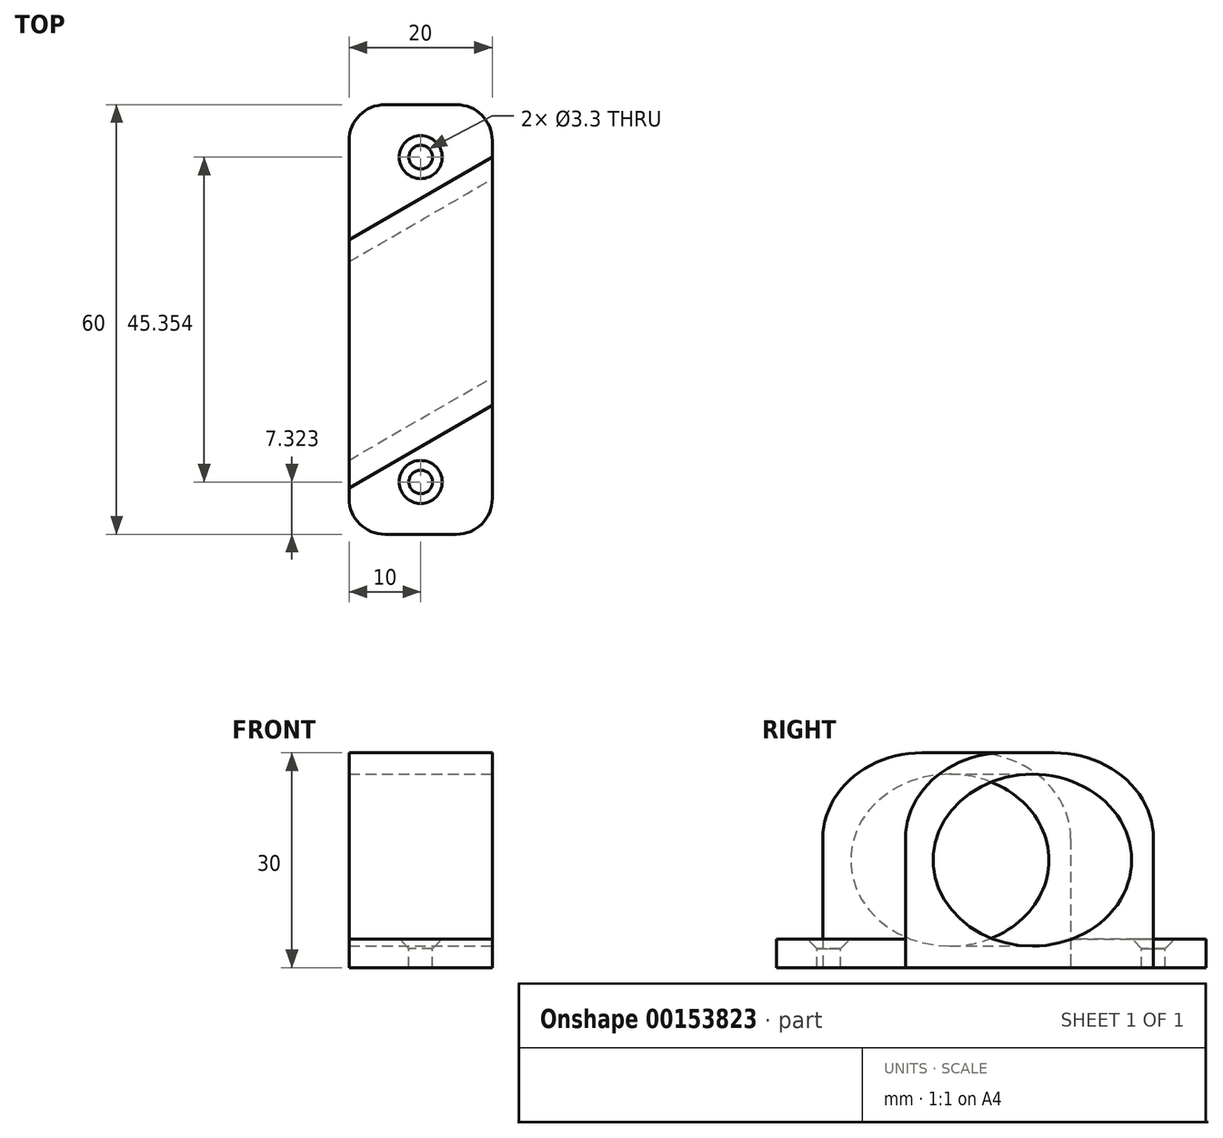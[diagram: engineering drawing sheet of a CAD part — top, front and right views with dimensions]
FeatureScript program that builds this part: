
annotation { "Feature Type Name" : "Feature", "Feature Type Description" : "" }
export const myFeature = defineFeature(function(context is Context, id is Id, definition is map)
    precondition{}
    {
        {
            var Q0;
            Q0=qCreatedBy(makeId("Top.planeOp"),FACE);
            var sketch = newSketch(context, id + "F0", { "sketchPlane" : qUnion([Q0])});
            skLineSegment(sketch, "E0.bottom", {"start": v(-10, 30) * mm, "end": v(10, 30) * mm});
            skLineSegment(sketch, "E0.top", {"start": v(-10, -30) * mm, "end": v(10, -30) * mm});
            skLineSegment(sketch, "E0.left", {"start": v(-10, 30) * mm, "end": v(-10, -30) * mm});
            skLineSegment(sketch, "E0.right", {"start": v(10, 30) * mm, "end": v(10, -30) * mm});
            skPoint(sketch, "E0.middle", {"position": v(0, 0) * mm});
            skLineSegment(sketch, "E1", {"start": v(-10, 11.13) * mm, "end": v(10, 22.68) * mm});
            skLineSegment(sketch, "E2", {"start": v(10, -11.96) * mm, "end": v(-10, -23.51) * mm});
            skPoint(sketch, "E3.orphan", {"position": v(-29.28, 0) * mm});
            skPoint(sketch, "E4.orphan", {"position": v(-29.28, -34.64) * mm});
            skSolve(sketch);
        }
        {
            var Q0;
            {var subQ0=sQuery(id+"F0.wireOp",EDGE,"E0.bottom");Q0=makeQuery(id+"F0.imprint","IMPRINT",FACE,{"disambiguationData":[TD([[makeQuery(id+"F0.imprint","IMPRINT",EDGE,{"derivedFrom":subQ0}),-1.0]])]});}
            var Q1;
            {var subQ0=sQuery(id+"F0.wireOp",EDGE,"E0.top");Q1=makeQuery(id+"F0.imprint","IMPRINT",FACE,{"disambiguationData":[TD([[makeQuery(id+"F0.imprint","IMPRINT",EDGE,{"derivedFrom":subQ0}),1.0]])]});}
            extrude(context, id + "F1", {"entities" : qUnion([Q0, Q1]), "depth" : 4 * mm});
        }
        {
            var Q0;
            {var subQ0=sQuery(id+"F0.wireOp",EDGE,"E1");Q0=makeQuery(id+"F0.imprint","IMPRINT",FACE,{"disambiguationData":[TD([[makeQuery(id+"F0.imprint","IMPRINT",EDGE,{"derivedFrom":subQ0}),-1.0]])]});}
            extrude(context, id + "F2", {"entities" : qUnion([Q0]), "depth" : 30 * mm});
        }
        {
            var Q0;
            Q0=makeQuery(id+"F2.opExtrude","SWEPT_FACE",FACE,{"disambiguationData":[OSD([sQuery(id+"F0.wireOp",EDGE,"E1")])]});
            var sketch = newSketch(context, id + "F3", { "sketchPlane" : qUnion([Q0])});
            skLineSegment(sketch, "E5.bottom", {"start": v(-20, 15.59) * mm, "end": v(-1.97, 15.59) * mm});
            skLineSegment(sketch, "E5.top", {"start": v(-20, 27.37) * mm, "end": v(-1.97, 27.37) * mm});
            skLineSegment(sketch, "E5.left", {"start": v(-20, 15.59) * mm, "end": v(-20, 27.37) * mm});
            skLineSegment(sketch, "E5.right", {"start": v(-1.97, 15.59) * mm, "end": v(-1.97, 27.37) * mm});
            skPoint(sketch, "E5.middle", {"position": v(-10.98, 21.48) * mm});
            skSolve(sketch);
        }
        {
            var Q0;
            Q0=makeQuery(id+"F3.imprint","IMPRINT",FACE,{"disambiguationData":[TD([[makeQuery(id+"F3.imprint","IMPRINT",EDGE,{"derivedFrom":sQuery(id+"F3.wireOp",EDGE,"E5.bottom")}),1.0]])]});
            extrude(context, id + "F4", {"entities" : qUnion([Q0]), "operationType" : NewBodyOperationType.ADD, "depth" : 25 * mm});
        }
        {
            var Q0;
            Q0=makeQuery(id+"F4.opExtrude","SWEPT_FACE",FACE,{"disambiguationData":[OSD([sQuery(id+"F3.wireOp",EDGE,"E5.left")])]});
            cPlane(context, id + "F5", {"entities" : qUnion([Q0]), "cplaneType" : CPlaneType.OFFSET, "offset" : 0 * mm, "width" : 150 * mm, "height" : 150 * mm});
        }
        {
            var Q0;
            Q0=qCreatedBy(id+"F5.planeOp",FACE);
            var sketch = newSketch(context, id + "F6", { "sketchPlane" : qUnion([Q0])});
            skLineSegment(sketch, "E6", {"start": v(0, 0) * mm, "end": v(0, 30) * mm, "construction": true});
            skLineSegment(sketch, "E7.0", {"start": v(14.64, 30) * mm, "end": v(-15.36, 30) * mm});
            skPoint(sketch, "E8", {"position": v(0, 15) * mm});
            skCircle(sketch, "E9", {"center": v(0, 15) * mm, "radius": 12 * mm});
            skSolve(sketch);
        }
        {
            var Q0;
            Q0=qSketchRegion(id+"F6",true);
            extrude(context, id + "F7", {"entities" : qUnion([Q0]), "operationType" : NewBodyOperationType.REMOVE, "oppositeDirection" : true, "depth" : 67.5 * mm, "hasSecondDirection" : true, "secondDirectionOppositeDirection" : false, "secondDirectionDepth" : 25 * mm});
        }
        {
            var Q0;
            Q0=makeQuery(id+"F4.opExtrude","SWEPT_FACE",FACE,{"disambiguationData":[OSD([sQuery(id+"F3.wireOp",EDGE,"E5.left")])]});
            extrude(context, id + "F8", {"entities" : qUnion([Q0]), "operationType" : NewBodyOperationType.REMOVE, "oppositeDirection" : true, "depth" : 25 * mm});
        }
        {
            var Q0;
            Q0=makeQuery(id+"F1.opExtrude","CAP_FACE",FACE,{"disambiguationData":[OSD([sQuery(id+"F0.wireOp",EDGE,"E0.bottom"),sQuery(id+"F0.wireOp",EDGE,"E0.left"),sQuery(id+"F0.wireOp",EDGE,"E0.right"),sQuery(id+"F0.wireOp",EDGE,"E1")])],"isStart":false});
            var sketch = newSketch(context, id + "F9", { "sketchPlane" : qUnion([Q0])});
            skLineSegment(sketch, "E10", {"start": v(10, 22.68) * mm, "end": v(-10, 22.68) * mm, "construction": true});
            skPoint(sketch, "E11", {"position": v(0, 22.68) * mm});
            skPoint(sketch, "E12.MirrorP", {"position": v(0, -22.68) * mm});
            skSolve(sketch);
        }
        {
            var Q0;
            Q0=sQuery(id+"F9.wireOp",VERTEX,"E11");
            var Q1;
            Q1=sQuery(id+"F9.wireOp",VERTEX,"E12.MirrorP");
            var Q2;
            Q2=makeQuery(id+"F1.opExtrude","SWEPT_BODY",BODY,{"disambiguationData":[OSD([sQuery(id+"F0.wireOp",EDGE,"E0.bottom"),sQuery(id+"F0.wireOp",EDGE,"E0.left"),sQuery(id+"F0.wireOp",EDGE,"E0.right"),sQuery(id+"F0.wireOp",EDGE,"E1")])]});
            var Q3;
            Q3=makeQuery(id+"F1.opExtrude","SWEPT_BODY",BODY,{"disambiguationData":[OSD([sQuery(id+"F0.wireOp",EDGE,"E0.top"),sQuery(id+"F0.wireOp",EDGE,"E0.left"),sQuery(id+"F0.wireOp",EDGE,"E0.right"),sQuery(id+"F0.wireOp",EDGE,"E2")])]});
            hole(context, id + "F10", {"style" : HoleStyle.C_SINK, "endStyle" : HoleEndStyle.THROUGH, "holeDiameter" : 3.3 * mm, "cSinkDiameter" : 6 * mm, "cSinkAngle" : 90 * degree, "locations" : qUnion([Q0, Q1]), "scope" : qUnion([Q2, Q3]), "isTappedThrough" : true});
        }
        {
            var Q0;
            Q0=makeQuery(id+"F1.opExtrude","SWEPT_EDGE",EDGE,{"disambiguationData":[OSD([sQuery(id+"F0.wireOp",EDGE,"E0.bottom"),sQuery(id+"F0.wireOp",EDGE,"E0.left")])]});
            var Q1;
            Q1=makeQuery(id+"F1.opExtrude","SWEPT_EDGE",EDGE,{"disambiguationData":[OSD([sQuery(id+"F0.wireOp",EDGE,"E0.bottom"),sQuery(id+"F0.wireOp",EDGE,"E0.right")])]});
            var Q2;
            Q2=makeQuery(id+"F1.opExtrude","SWEPT_EDGE",EDGE,{"disambiguationData":[OSD([sQuery(id+"F0.wireOp",EDGE,"E0.top"),sQuery(id+"F0.wireOp",EDGE,"E0.right")])]});
            var Q3;
            Q3=makeQuery(id+"F1.opExtrude","SWEPT_EDGE",EDGE,{"disambiguationData":[OSD([sQuery(id+"F0.wireOp",EDGE,"E0.top"),sQuery(id+"F0.wireOp",EDGE,"E0.left")])]});
            fillet(context, id + "F11", {"entities" : qUnion([Q0, Q1, Q2, Q3]), "radius" : 5 * mm, "tangentPropagation" : true, "allowEdgeOverflow" : false});
        }
        {
            var Q0;
            Q0=makeQuery(id+"F2.opExtrude","CAP_EDGE",EDGE,{"disambiguationData":[OSD([sQuery(id+"F0.wireOp",EDGE,"E1")])],"isStart":false});
            var Q1;
            Q1=makeQuery(id+"F2.opExtrude","CAP_EDGE",EDGE,{"disambiguationData":[OSD([sQuery(id+"F0.wireOp",EDGE,"E2")])],"isStart":false});
            fillet(context, id + "F12", {"entities" : qUnion([Q0, Q1]), "radius" : 12 * mm, "tangentPropagation" : true, "allowEdgeOverflow" : false});
        }
    });
